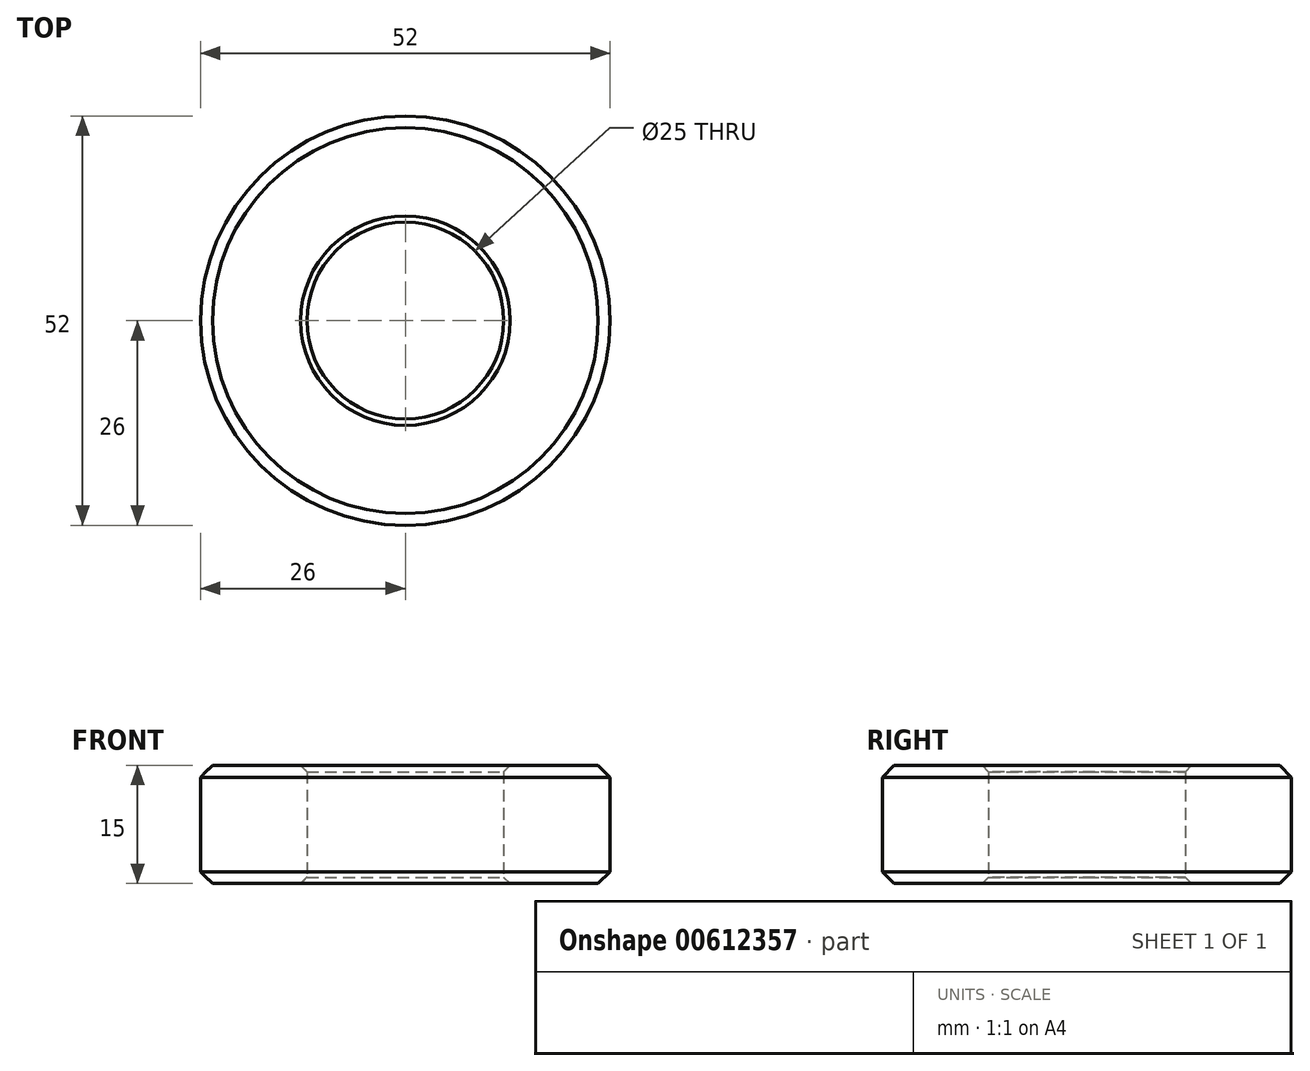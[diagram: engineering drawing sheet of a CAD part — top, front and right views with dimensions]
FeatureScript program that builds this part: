
annotation { "Feature Type Name" : "Feature", "Feature Type Description" : "" }
export const myFeature = defineFeature(function(context is Context, id is Id, definition is map)
    precondition{}
    {
        {
            var Q0;
            Q0=qCreatedBy(makeId("Front.planeOp"),FACE);
            var sketch = newSketch(context, id + "F0", { "sketchPlane" : qUnion([Q0])});
            skLineSegment(sketch, "E0", {"start": v(0, 0) * mm, "end": v(0, 23.76) * mm});
            skLineSegment(sketch, "E1.bottom", {"start": v(12.5, 0) * mm, "end": v(26, 0) * mm});
            skLineSegment(sketch, "E1.top", {"start": v(12.5, 15) * mm, "end": v(26, 15) * mm});
            skLineSegment(sketch, "E1.left", {"start": v(12.5, 0) * mm, "end": v(12.5, 15) * mm});
            skLineSegment(sketch, "E1.right", {"start": v(26, 0) * mm, "end": v(26, 15) * mm});
            skSolve(sketch);
        }
        {
            var Q0;
            Q0=makeQuery(id+"F0.imprint","IMPRINT",FACE,{"disambiguationData":[TD([[makeQuery(id+"F0.imprint","IMPRINT",EDGE,{"derivedFrom":sQuery(id+"F0.wireOp",EDGE,"E1.bottom")}),1.0]])]});
            var Q1;
            Q1=sQuery(id+"F0.wireOp",EDGE,"E0");
            revolve(context, id + "F1", {"entities" : qUnion([Q0]), "axis" : qUnion([Q1]), "revolveType" : RevolveType.FULL});
        }
        {
            var Q0;
            Q0=makeQuery(id+"F1.opRevolve","SWEPT_EDGE",EDGE,{"disambiguationData":[OSD([sQuery(id+"F0.wireOp",EDGE,"E1.top"),sQuery(id+"F0.wireOp",EDGE,"E1.right")])]});
            var Q1;
            Q1=makeQuery(id+"F1.opRevolve","SWEPT_EDGE",EDGE,{"disambiguationData":[OSD([sQuery(id+"F0.wireOp",EDGE,"E1.bottom"),sQuery(id+"F0.wireOp",EDGE,"E1.right")])]});
            chamfer(context, id + "F2", {"entities" : qUnion([Q0, Q1]), "width" : 1.5 * mm, "tangentPropagation" : true});
        }
        {
            var Q0;
            Q0=makeQuery(id+"F1.opRevolve","SWEPT_EDGE",EDGE,{"disambiguationData":[OSD([sQuery(id+"F0.wireOp",EDGE,"E1.top"),sQuery(id+"F0.wireOp",EDGE,"E1.left")])]});
            var Q1;
            Q1=makeQuery(id+"F1.opRevolve","SWEPT_EDGE",EDGE,{"disambiguationData":[OSD([sQuery(id+"F0.wireOp",EDGE,"E1.bottom"),sQuery(id+"F0.wireOp",EDGE,"E1.left")])]});
            chamfer(context, id + "F3", {"entities" : qUnion([Q0, Q1]), "width" : 0.8 * mm, "tangentPropagation" : true});
        }
    });
